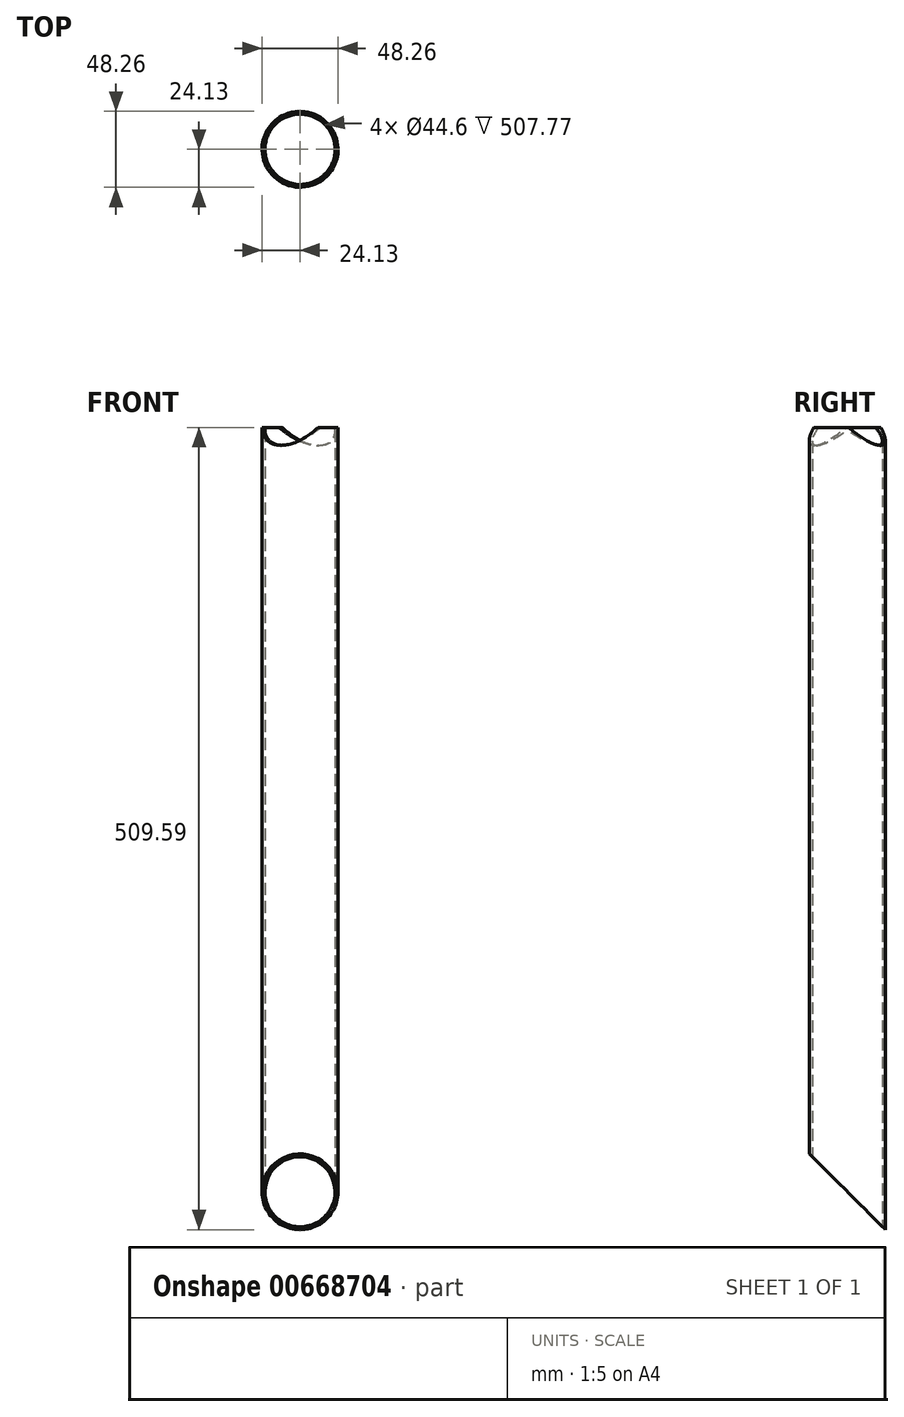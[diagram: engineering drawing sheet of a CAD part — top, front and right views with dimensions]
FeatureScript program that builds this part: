
annotation { "Feature Type Name" : "Feature", "Feature Type Description" : "" }
export const myFeature = defineFeature(function(context is Context, id is Id, definition is map)
    precondition{}
    {
        {
            var Q0;
            Q0=qCreatedBy(makeId("Top.planeOp"),FACE);
            var sketch = newSketch(context, id + "F0", { "sketchPlane" : qUnion([Q0])});
            skCircle(sketch, "E0", {"center": v(0, 0) * mm, "radius": 24.13 * mm});
            skCircle(sketch, "E1.0", {"center": v(0, 0) * mm, "radius": 22.3 * mm});
            skSolve(sketch);
        }
        {
            var Q0;
            Q0=qSketchRegion(id+"F0",true);
            extrude(context, id + "F1", {"entities" : qUnion([Q0]), "depth" : 509.59 * mm, "offsetDistance" : 25.4 * mm});
        }
        {
            var Q0;
            Q0=qCreatedBy(makeId("Right.planeOp"),FACE);
            var sketch = newSketch(context, id + "F2", { "sketchPlane" : qUnion([Q0])});
            skLineSegment(sketch, "E2.bottom", {"start": v(-24.13, 0) * mm, "end": v(24.13, 0) * mm});
            skLineSegment(sketch, "E2.left", {"start": v(-24.13, 0) * mm, "end": v(-24.13, 48.26) * mm});
            skLineSegment(sketch, "E3", {"start": v(-24.13, 48.26) * mm, "end": v(24.13, 0) * mm});
            skSolve(sketch);
        }
        {
            var Q0;
            Q0=qSketchRegion(id+"F2",true);
            extrude(context, id + "F3", {"entities" : qUnion([Q0]), "operationType" : NewBodyOperationType.REMOVE, "endBound" : BoundingType.THROUGH_ALL, "oppositeDirection" : true, "depth" : 25.4 * mm, "offsetDistance" : 25.4 * mm, "hasSecondDirection" : true, "secondDirectionBound" : SecondDirectionBoundingType.THROUGH_ALL, "secondDirectionOppositeDirection" : false, "secondDirectionDepth" : 25.4 * mm});
        }
        {
            var Q0;
            Q0=makeQuery(id+"F1.opExtrude","CAP_FACE",FACE,{"disambiguationData":[OSD([sQuery(id+"F0.wireOp",EDGE,"E0"),sQuery(id+"F0.wireOp",EDGE,"E1.0")])],"isStart":false});
            var sketch = newSketch(context, id + "F4", { "sketchPlane" : qUnion([Q0])});
            skLineSegment(sketch, "E4", {"start": v(12.07, 20.9) * mm, "end": v(-12.07, -20.9) * mm});
            skSolve(sketch);
        }
        {
            var Q0;
            Q0=sQuery(id+"F4.wireOp",EDGE,"E4");
            cPlane(context, id + "F5", {"entities" : qUnion([Q0]), "cplaneType" : CPlaneType.MID_PLANE, "offset" : 25.4 * mm, "width" : 152.4 * mm, "height" : 152.4 * mm});
        }
        {
            var Q0;
            Q0=qCreatedBy(id+"F5.planeOp",FACE);
            var sketch = newSketch(context, id + "F6", { "sketchPlane" : qUnion([Q0])});
            skCircle(sketch, "E5", {"center": v(0, 522.29) * mm, "radius": 24.13 * mm});
            skPoint(sketch, "E6", {"position": v(0, 509.59) * mm});
            skSolve(sketch);
        }
        {
            var Q0;
            Q0=qSketchRegion(id+"F6",true);
            extrude(context, id + "F7", {"entities" : qUnion([Q0]), "operationType" : NewBodyOperationType.REMOVE, "oppositeDirection" : true, "depth" : 50.8 * mm, "offsetDistance" : 25.4 * mm, "hasSecondDirection" : true, "secondDirectionOppositeDirection" : false, "secondDirectionDepth" : 50.8 * mm});
        }
    });
